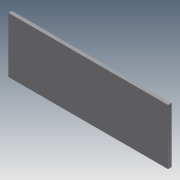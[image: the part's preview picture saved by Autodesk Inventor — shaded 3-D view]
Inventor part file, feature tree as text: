
AUTODESK INVENTOR PART (.ipt)
format: ipt  version: 2011 (Build 150239000, 239)  size: 66,048 bytes
history: native  units: in
note: dims shown in document units (in); Inventor stores cm internally (conversion verified against a paired STEP export)
features: extrude x1, sketch x1
ambient origin geometry x8: Origin, YZ Plane, XZ Plane, XY Plane, X Axis, Y Axis, Z Axis, Center Point
bodies: Solid1 (feature_tree)
feature tree (2):
  extrude  "Extrusion1"  Depth=4.0in
  sketch  "Sketch1"  dims[d0=11.5in d1=4.0in d2=0.25in d3=0.0in]
